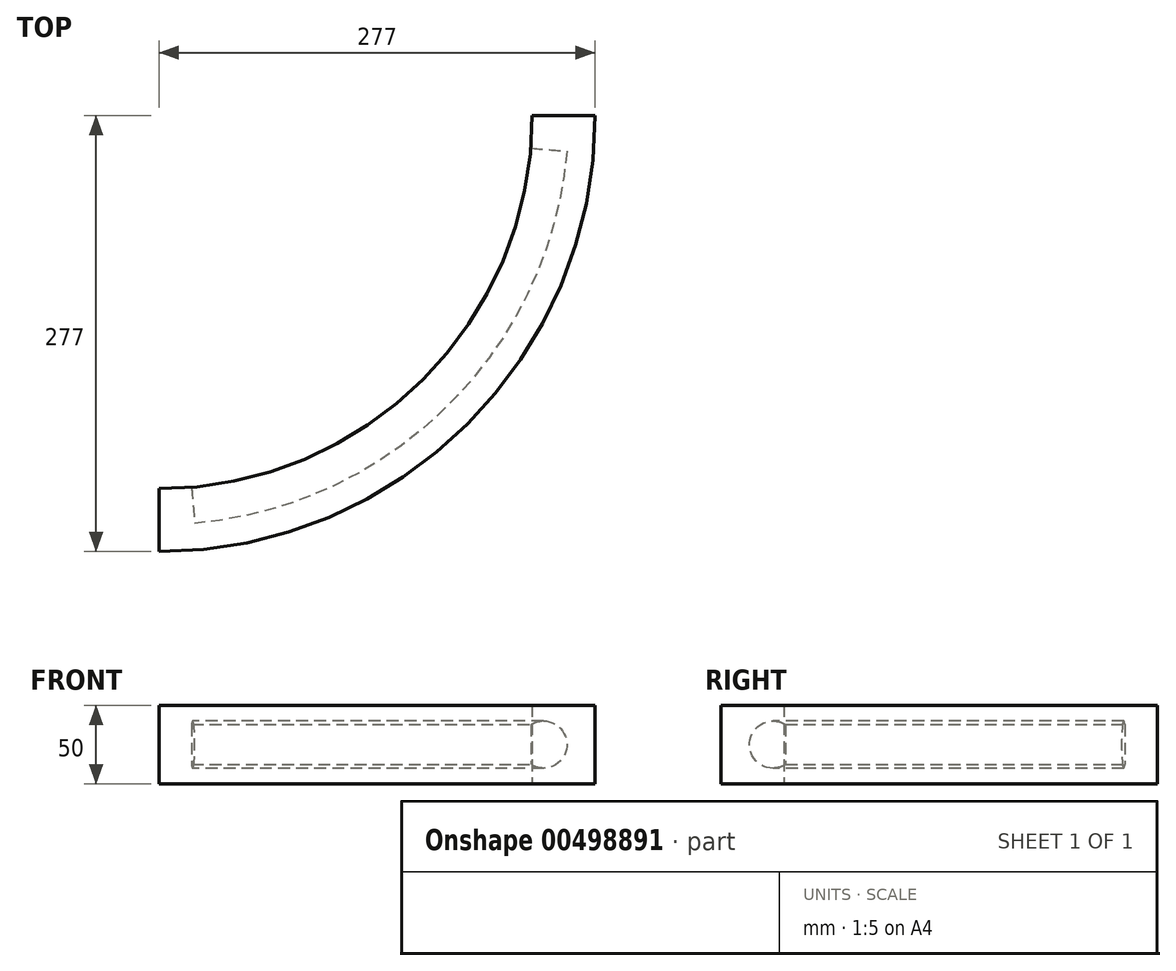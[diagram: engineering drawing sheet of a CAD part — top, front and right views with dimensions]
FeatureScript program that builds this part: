
annotation { "Feature Type Name" : "Feature", "Feature Type Description" : "" }
export const myFeature = defineFeature(function(context is Context, id is Id, definition is map)
    precondition{}
    {
        {
            var Q0;
            Q0=qCreatedBy(makeId("Front.planeOp"),FACE);
            var sketch = newSketch(context, id + "F0", { "sketchPlane" : qUnion([Q0])});
            skLineSegment(sketch, "E0.bottom", {"start": v(-8, 25) * mm, "end": v(32, 25) * mm});
            skLineSegment(sketch, "E0.top", {"start": v(-8, -25) * mm, "end": v(32, -25) * mm});
            skLineSegment(sketch, "E0.left", {"start": v(-8, 25) * mm, "end": v(-8, 12.69) * mm});
            skLineSegment(sketch, "E0.right", {"start": v(32, 25) * mm, "end": v(32, -25) * mm});
            skArc(sketch, "E1", {"start": v(-8, -12.69) * mm, "mid": v(15, 0) * mm, "end": v(-8, 12.69) * mm});
            skLineSegment(sketch, "E2.trimOffspring", {"start": v(-8, -12.69) * mm, "end": v(-8, -25) * mm});
            skLineSegment(sketch, "E3", {"start": v(-245, 45.88) * mm, "end": v(-245, -58.41) * mm});
            skSolve(sketch);
        }
        {
            var Q0;
            Q0=makeQuery(id+"F0.imprint","IMPRINT",FACE,{"disambiguationData":[TD([[makeQuery(id+"F0.imprint","IMPRINT",EDGE,{"derivedFrom":sQuery(id+"F0.wireOp",EDGE,"E0.bottom")}),-1.0]])]});
            var Q1;
            Q1=sQuery(id+"F0.wireOp",EDGE,"E3");
            revolve(context, id + "F1", {"entities" : qUnion([Q0]), "axis" : qUnion([Q1]), "revolveType" : RevolveType.ONE_DIRECTION, "angle" : 90 * degree});
        }
        {
            var Q0;
            Q0=makeQuery(id+"F1.opRevolve","CAP_FACE",FACE,{"disambiguationData":[OSD([sQuery(id+"F0.wireOp",EDGE,"E0.bottom"),sQuery(id+"F0.wireOp",EDGE,"E0.top"),sQuery(id+"F0.wireOp",EDGE,"E0.left"),sQuery(id+"F0.wireOp",EDGE,"E0.right"),sQuery(id+"F0.wireOp",EDGE,"E1"),sQuery(id+"F0.wireOp",EDGE,"E2.trimOffspring")])],"isStart":true});
            var sketch = newSketch(context, id + "F2", { "sketchPlane" : qUnion([Q0])});
            skLineSegment(sketch, "E4.bottom", {"start": v(-32, 25) * mm, "end": v(8, 25) * mm});
            skLineSegment(sketch, "E4.top", {"start": v(-32, -25) * mm, "end": v(8, -25) * mm});
            skLineSegment(sketch, "E4.left", {"start": v(-32, 25) * mm, "end": v(-32, -25) * mm});
            skLineSegment(sketch, "E4.right", {"start": v(8, 25) * mm, "end": v(8, -25) * mm});
            skLineSegment(sketch, "E5", {"start": v(245, -49.86) * mm, "end": v(245, 57.79) * mm});
            skSolve(sketch);
        }
        {
            var Q0;
            Q0 = qSketchRegion(id + "F2", true);
            var Q1;
            Q1=sQuery(id+"F2.wireOp",EDGE,"E5");
            revolve(context, id + "F3", {"operationType" : NewBodyOperationType.ADD, "entities" : qUnion([Q0]), "axis" : qUnion([Q1]), "revolveType" : RevolveType.TWO_DIRECTIONS, "angle" : 0 * degree, "angleBack" : 355 * degree});
        }
        {
            var Q0;
            Q0=makeQuery(id+"F1.opRevolve","CAP_FACE",FACE,{"disambiguationData":[OSD([sQuery(id+"F0.wireOp",EDGE,"E0.bottom"),sQuery(id+"F0.wireOp",EDGE,"E0.top"),sQuery(id+"F0.wireOp",EDGE,"E0.left"),sQuery(id+"F0.wireOp",EDGE,"E0.right"),sQuery(id+"F0.wireOp",EDGE,"E1"),sQuery(id+"F0.wireOp",EDGE,"E2.trimOffspring")])],"isStart":false});
            var sketch = newSketch(context, id + "F4", { "sketchPlane" : qUnion([Q0])});
            skLineSegment(sketch, "E6.bottom", {"start": v(277, -25) * mm, "end": v(237, -25) * mm});
            skLineSegment(sketch, "E6.top", {"start": v(277, 25) * mm, "end": v(237, 25) * mm});
            skLineSegment(sketch, "E6.left", {"start": v(277, -25) * mm, "end": v(277, 25) * mm});
            skLineSegment(sketch, "E6.right", {"start": v(237, -25) * mm, "end": v(237, 25) * mm});
            skLineSegment(sketch, "E7", {"start": v(0, 24.64) * mm, "end": v(0, -27.38) * mm});
            skSolve(sketch);
        }
        {
            var Q0;
            Q0 = qSketchRegion(id + "F4", true);
            var Q1;
            Q1=sQuery(id+"F4.wireOp",EDGE,"E7");
            revolve(context, id + "F5", {"operationType" : NewBodyOperationType.ADD, "entities" : qUnion([Q0]), "axis" : qUnion([Q1]), "revolveType" : RevolveType.TWO_DIRECTIONS, "angle" : 360 * degree, "angleBack" : 355 * degree});
        }
    });
